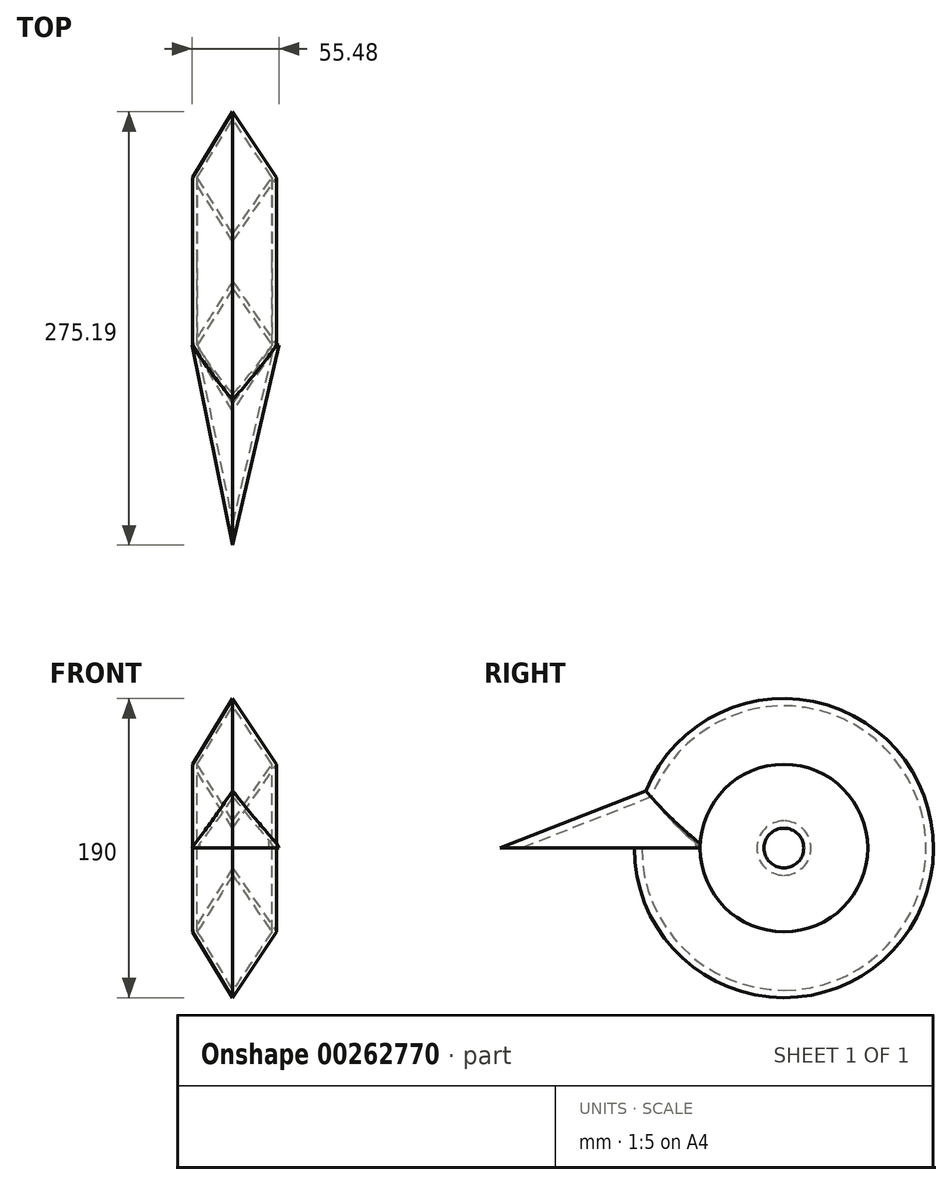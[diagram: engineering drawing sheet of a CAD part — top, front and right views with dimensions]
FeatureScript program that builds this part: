
annotation { "Feature Type Name" : "Feature", "Feature Type Description" : "" }
export const myFeature = defineFeature(function(context is Context, id is Id, definition is map)
    precondition{}
    {
        {
            var Q0;
            Q0=qCreatedBy(makeId("Top.planeOp"),FACE);
            var sketch = newSketch(context, id + "F0", { "sketchPlane" : qUnion([Q0])});
            skLineSegment(sketch, "E0", {"start": v(0, 0) * mm, "end": v(0, 40.57) * mm});
            skLineSegment(sketch, "E1", {"start": v(0, 40.57) * mm, "end": v(28, 0) * mm});
            skLineSegment(sketch, "E2", {"start": v(28, 0) * mm, "end": v(0, -41.8) * mm});
            skLineSegment(sketch, "E3", {"start": v(0, -41.8) * mm, "end": v(-25.47, 0) * mm});
            skLineSegment(sketch, "E4", {"start": v(-25.47, 0) * mm, "end": v(0, 40.57) * mm});
            skSolve(sketch);
        }
        {
            var Q0;
            Q0=qCreatedBy(makeId("Top.planeOp"),FACE);
            var sketch = newSketch(context, id + "F1", { "sketchPlane" : qUnion([Q0])});
            skLineSegment(sketch, "E5", {"start": v(-54.98, 53.2) * mm, "end": v(55.75, 53.2) * mm, "construction": true});
            skSolve(sketch);
        }
        {
            var Q0;
            Q0 = qSketchRegion(id + "F0", true);
            var Q1;
            Q1=sQuery(id+"F1.wireOp",EDGE,"E5");
            revolve(context, id + "F2", {"entities" : qUnion([Q0]), "axis" : qUnion([Q1]), "revolveType" : RevolveType.FULL});
        }
        {
            var Q0;
            Q0=qCreatedBy(makeId("Front.planeOp"),FACE);
            cPlane(context, id + "F3", {"entities" : qUnion([Q0]), "cplaneType" : CPlaneType.OFFSET, "offset" : 127 * mm, "width" : 152.4 * mm, "height" : 152.4 * mm});
        }
        {
            var Q0;
            Q0=qCreatedBy(id+"F3.planeOp",FACE);
            var sketch = newSketch(context, id + "F4", { "sketchPlane" : qUnion([Q0])});
            skPoint(sketch, "E6", {"position": v(0, 0) * mm});
            skSolve(sketch);
        }
        {
            var Q0;
            Q0=qCreatedBy(makeId("Front.planeOp"),FACE);
            var sketch = newSketch(context, id + "F5", { "sketchPlane" : qUnion([Q0])});
            skLineSegment(sketch, "E7", {"start": v(0, 49.97) * mm, "end": v(-25.84, 0) * mm});
            skLineSegment(sketch, "E8", {"start": v(0, 49.97) * mm, "end": v(29.64, 0) * mm});
            skLineSegment(sketch, "E9", {"start": v(29.64, 0) * mm, "end": v(-25.84, 0) * mm});
            skSolve(sketch);
        }
        {
            var Q1;
            Q1=sQuery(id+"F4.wireOp",VERTEX,"E6");
            var Q2;
            Q2 = qSketchRegion(id + "F5", true);
            loft(context, id + "F6", {"operationType" : NewBodyOperationType.ADD, "sheetProfilesArray" : [{ "sheetProfileEntities" : qUnion([Q1]) }, { "sheetProfileEntities" : qUnion([Q2]) }]});
        }
        {
            var Q0;
            {var subQ0=sQuery(id+"F5.wireOp",EDGE,"E9");var subQ1=sQuery(id+"F5.wireOp",EDGE,"E8");var subQ2=sQuery(id+"F5.wireOp",EDGE,"E7");Q0=makeQuery(id+"F6.opLoft","SWEPT_FACE",FACE,{"disambiguationData":[OSD([subQ2,subQ1,subQ0]),TDD([makeQuery(id+"F5.imprint","INTERSECT",VERTEX,{"derivedFrom":[subQ2,subQ0]}),makeQuery(id+"F5.imprint","INTERSECT",VERTEX,{"derivedFrom":[subQ1,subQ0]}),makeQuery(id+"F5.imprint","IMPRINT",EDGE,{"derivedFrom":subQ0})])]});}
            shell(context, id + "F7", {"entities" : qUnion([Q0]), "thickness" : 2.54 * mm});
        }
    });
